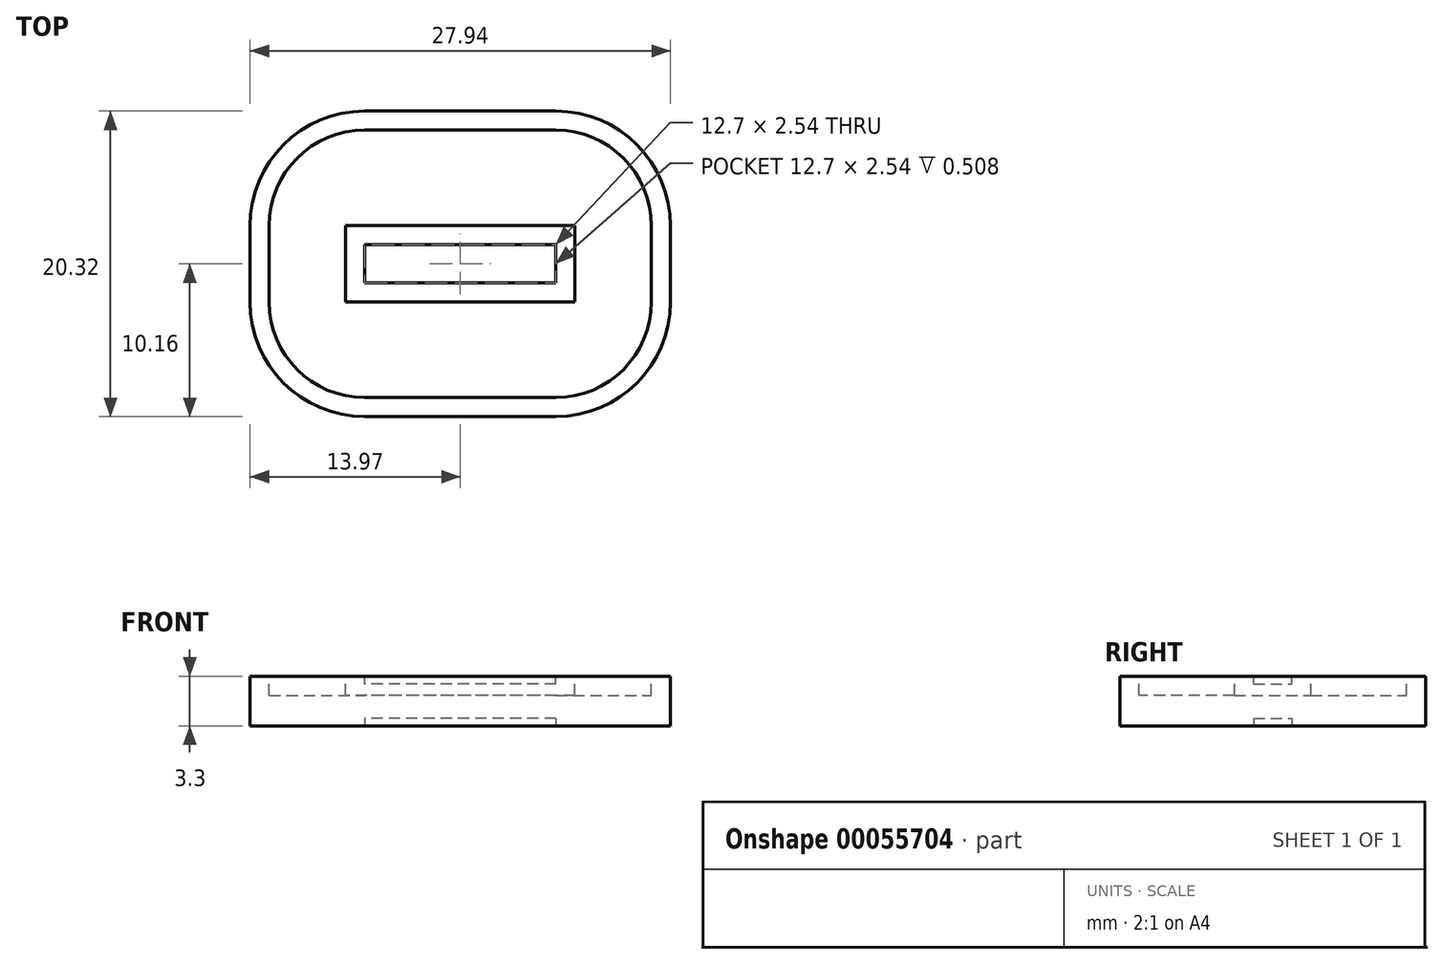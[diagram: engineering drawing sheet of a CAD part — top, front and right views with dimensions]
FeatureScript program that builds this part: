
annotation { "Feature Type Name" : "Feature", "Feature Type Description" : "" }
export const myFeature = defineFeature(function(context is Context, id is Id, definition is map)
    precondition{}
    {
        {
            var Q0;
            Q0=qCreatedBy(makeId("Top.planeOp"),FACE);
            var sketch = newSketch(context, id + "F0", { "sketchPlane" : qUnion([Q0])});
            skLineSegment(sketch, "E0.rect.bottom", {"start": v(6.35, -10.16) * mm, "end": v(-6.35, -10.16) * mm});
            skLineSegment(sketch, "E0.rect.top", {"start": v(6.35, 10.16) * mm, "end": v(-6.35, 10.16) * mm});
            skLineSegment(sketch, "E0.rect.left", {"start": v(13.97, -2.54) * mm, "end": v(13.97, 2.54) * mm});
            skLineSegment(sketch, "E0.rect.right", {"start": v(-13.97, -2.54) * mm, "end": v(-13.97, 2.54) * mm});
            skPoint(sketch, "E0.rect.middle", {"position": v(0, 0) * mm});
            skLineSegment(sketch, "E1.rect.bottom", {"start": v(6.35, -1.27) * mm, "end": v(-6.35, -1.27) * mm});
            skLineSegment(sketch, "E1.rect.top", {"start": v(6.35, 1.27) * mm, "end": v(-6.35, 1.27) * mm});
            skLineSegment(sketch, "E1.rect.left", {"start": v(6.35, -1.27) * mm, "end": v(6.35, 1.27) * mm});
            skLineSegment(sketch, "E1.rect.right", {"start": v(-6.35, -1.27) * mm, "end": v(-6.35, 1.27) * mm});
            skPoint(sketch, "E2.visualSharp", {"position": v(-13.97, 10.16) * mm});
            skArc(sketch, "E2.filletArc", {"start": v(-6.35, 10.16) * mm, "mid": v(-11.74, 7.93) * mm, "end": v(-13.97, 2.54) * mm});
            skPoint(sketch, "E3.visualSharp", {"position": v(13.97, 10.16) * mm});
            skArc(sketch, "E3.filletArc", {"start": v(13.97, 2.54) * mm, "mid": v(11.74, 7.93) * mm, "end": v(6.35, 10.16) * mm});
            skPoint(sketch, "E4.visualSharp", {"position": v(13.97, -10.16) * mm});
            skArc(sketch, "E4.filletArc", {"start": v(6.35, -10.16) * mm, "mid": v(11.74, -7.93) * mm, "end": v(13.97, -2.54) * mm});
            skPoint(sketch, "E5.visualSharp", {"position": v(-13.97, -10.16) * mm});
            skArc(sketch, "E5.filletArc", {"start": v(-13.97, -2.54) * mm, "mid": v(-11.74, -7.93) * mm, "end": v(-6.35, -10.16) * mm});
            skSolve(sketch);
        }
        {
            var Q0;
            Q0=makeQuery(id+"F0.imprint","IMPRINT",FACE,{"disambiguationData":[TD([[makeQuery(id+"F0.imprint","IMPRINT",EDGE,{"derivedFrom":sQuery(id+"F0.wireOp",EDGE,"E0.rect.bottom")}),-1.0]])]});
            var Q1;
            Q1=makeQuery(id+"F0.imprint","IMPRINT",FACE,{"disambiguationData":[TD([[makeQuery(id+"F0.imprint","IMPRINT",EDGE,{"derivedFrom":sQuery(id+"F0.wireOp",EDGE,"E1.rect.bottom")}),-1.0]])]});
            extrude(context, id + "F1", {"entities" : qUnion([Q0, Q1]), "depth" : 3.3 * mm});
        }
        {
            var Q0;
            Q0=makeQuery(id+"F1.opExtrude","CAP_FACE",FACE,{"disambiguationData":[OSD([sQuery(id+"F0.wireOp",EDGE,"E0.rect.bottom"),sQuery(id+"F0.wireOp",EDGE,"E0.rect.top"),sQuery(id+"F0.wireOp",EDGE,"E0.rect.left"),sQuery(id+"F0.wireOp",EDGE,"E0.rect.right"),sQuery(id+"F0.wireOp",EDGE,"E1.rect.bottom"),sQuery(id+"F0.wireOp",EDGE,"E1.rect.top"),sQuery(id+"F0.wireOp",EDGE,"E1.rect.left"),sQuery(id+"F0.wireOp",EDGE,"E1.rect.right"),sQuery(id+"F0.wireOp",EDGE,"E2.filletArc"),sQuery(id+"F0.wireOp",EDGE,"E3.filletArc"),sQuery(id+"F0.wireOp",EDGE,"E4.filletArc"),sQuery(id+"F0.wireOp",EDGE,"E5.filletArc")])],"isStart":false});
            var sketch = newSketch(context, id + "F2", { "sketchPlane" : qUnion([Q0])});
            skLineSegment(sketch, "E6.rect.bottom", {"start": v(6.35, -10.16) * mm, "end": v(-6.35, -10.16) * mm});
            skLineSegment(sketch, "E6.rect.top", {"start": v(6.35, 10.16) * mm, "end": v(-6.35, 10.16) * mm});
            skLineSegment(sketch, "E6.rect.left", {"start": v(13.97, -2.54) * mm, "end": v(13.97, 2.54) * mm});
            skLineSegment(sketch, "E6.rect.right", {"start": v(-13.97, -2.54) * mm, "end": v(-13.97, 2.54) * mm});
            skPoint(sketch, "E6.rect.middle", {"position": v(0, 0) * mm});
            skPoint(sketch, "E7.visualSharp", {"position": v(-13.97, 10.16) * mm});
            skArc(sketch, "E7.filletArc", {"start": v(-6.35, 10.16) * mm, "mid": v(-11.74, 7.93) * mm, "end": v(-13.97, 2.54) * mm});
            skPoint(sketch, "E8.visualSharp", {"position": v(13.97, 10.16) * mm});
            skArc(sketch, "E8.filletArc", {"start": v(13.97, 2.54) * mm, "mid": v(11.74, 7.93) * mm, "end": v(6.35, 10.16) * mm});
            skPoint(sketch, "E9.visualSharp", {"position": v(13.97, -10.16) * mm});
            skArc(sketch, "E9.filletArc", {"start": v(6.35, -10.16) * mm, "mid": v(11.74, -7.93) * mm, "end": v(13.97, -2.54) * mm});
            skPoint(sketch, "E10.visualSharp", {"position": v(-13.97, -10.16) * mm});
            skArc(sketch, "E10.filletArc", {"start": v(-13.97, -2.54) * mm, "mid": v(-11.74, -7.93) * mm, "end": v(-6.35, -10.16) * mm});
            skLineSegment(sketch, "E11.rect.bottom", {"start": v(6.35, -1.27) * mm, "end": v(-6.35, -1.27) * mm});
            skLineSegment(sketch, "E11.rect.top", {"start": v(6.35, 1.27) * mm, "end": v(-6.35, 1.27) * mm});
            skLineSegment(sketch, "E11.rect.left", {"start": v(6.35, -1.27) * mm, "end": v(6.35, 1.27) * mm});
            skLineSegment(sketch, "E11.rect.right", {"start": v(-6.35, -1.27) * mm, "end": v(-6.35, 1.27) * mm});
            skLineSegment(sketch, "E12.rect.bottom", {"start": v(6.35, -8.9) * mm, "end": v(-6.35, -8.9) * mm});
            skLineSegment(sketch, "E12.rect.top", {"start": v(6.35, 8.9) * mm, "end": v(-6.35, 8.9) * mm});
            skLineSegment(sketch, "E12.rect.left", {"start": v(12.7, -2.54) * mm, "end": v(12.7, 2.54) * mm});
            skLineSegment(sketch, "E12.rect.right", {"start": v(-12.7, -2.54) * mm, "end": v(-12.7, 2.54) * mm});
            skPoint(sketch, "E13.visualSharp", {"position": v(-12.7, 8.89) * mm});
            skArc(sketch, "E13.filletArc", {"start": v(-6.35, 8.89) * mm, "mid": v(-10.84, 7.03) * mm, "end": v(-12.7, 2.54) * mm});
            skPoint(sketch, "E14.visualSharp", {"position": v(-12.7, -8.9) * mm});
            skArc(sketch, "E14.filletArc", {"start": v(-12.7, -2.54) * mm, "mid": v(-10.84, -7.03) * mm, "end": v(-6.35, -8.89) * mm});
            skPoint(sketch, "E15.visualSharp", {"position": v(12.7, -8.89) * mm});
            skArc(sketch, "E15.filletArc", {"start": v(6.35, -8.89) * mm, "mid": v(10.84, -7.03) * mm, "end": v(12.7, -2.54) * mm});
            skPoint(sketch, "E16.visualSharp", {"position": v(12.7, 8.9) * mm});
            skArc(sketch, "E16.filletArc", {"start": v(12.7, 2.54) * mm, "mid": v(10.84, 7.03) * mm, "end": v(6.35, 8.9) * mm});
            skLineSegment(sketch, "E17.rect.bottom", {"start": v(7.62, -2.54) * mm, "end": v(-7.62, -2.54) * mm});
            skLineSegment(sketch, "E17.rect.top", {"start": v(7.62, 2.54) * mm, "end": v(-7.62, 2.54) * mm});
            skLineSegment(sketch, "E17.rect.left", {"start": v(7.62, -2.54) * mm, "end": v(7.62, 2.54) * mm});
            skLineSegment(sketch, "E17.rect.right", {"start": v(-7.62, -2.54) * mm, "end": v(-7.62, 2.54) * mm});
            skSolve(sketch);
        }
        {
            var Q0;
            Q0=makeQuery(id+"F2.imprint","IMPRINT",FACE,{"disambiguationData":[TD([[makeQuery(id+"F2.imprint","IMPRINT",EDGE,{"derivedFrom":sQuery(id+"F2.wireOp",EDGE,"E12.rect.bottom")}),-1.0]])]});
            extrude(context, id + "F3", {"entities" : qUnion([Q0]), "operationType" : NewBodyOperationType.REMOVE, "oppositeDirection" : true, "depth" : 1.27 * mm});
        }
        {
            var Q0;
            Q0=makeQuery(id+"F2.imprint","IMPRINT",FACE,{"disambiguationData":[TD([[makeQuery(id+"F2.imprint","IMPRINT",EDGE,{"derivedFrom":sQuery(id+"F2.wireOp",EDGE,"E11.rect.bottom")}),-1.0]])]});
            extrude(context, id + "F4", {"entities" : qUnion([Q0]), "operationType" : NewBodyOperationType.REMOVE, "oppositeDirection" : true, "depth" : 0.5 * mm});
        }
        {
            var Q0;
            Q0=makeQuery(id+"F0.imprint","IMPRINT",FACE,{"disambiguationData":[TD([[makeQuery(id+"F0.imprint","IMPRINT",EDGE,{"derivedFrom":sQuery(id+"F0.wireOp",EDGE,"E1.rect.bottom")}),-1.0]])]});
            extrude(context, id + "F5", {"entities" : qUnion([Q0]), "operationType" : NewBodyOperationType.REMOVE, "depth" : 0.5 * mm});
        }
    });
